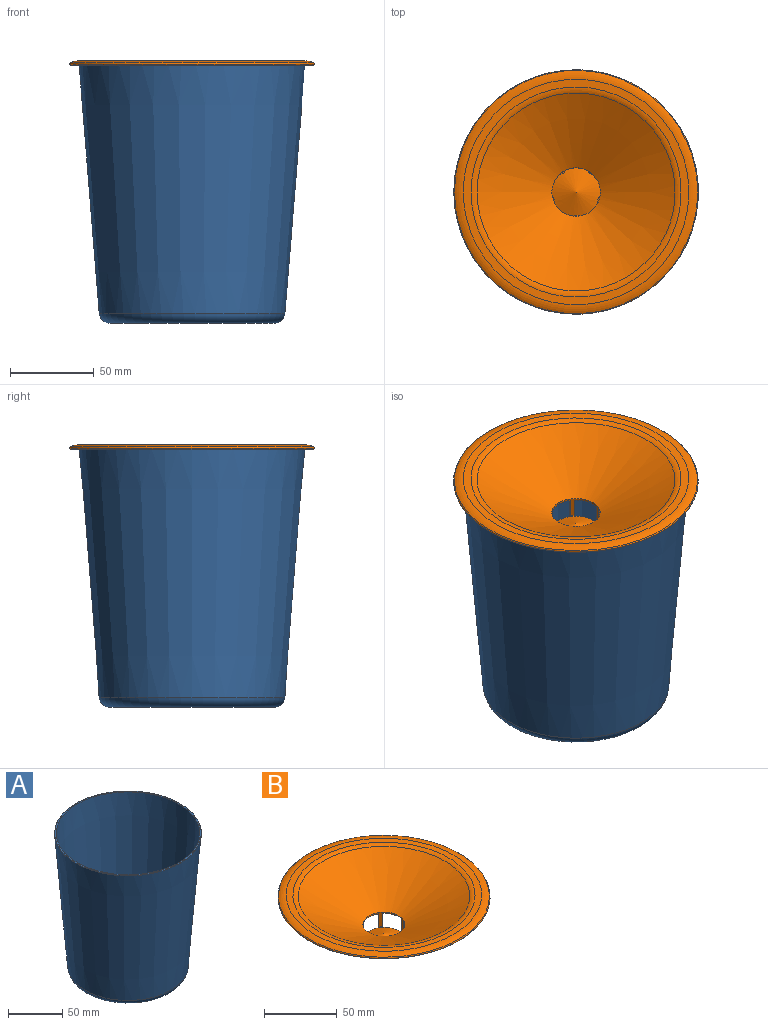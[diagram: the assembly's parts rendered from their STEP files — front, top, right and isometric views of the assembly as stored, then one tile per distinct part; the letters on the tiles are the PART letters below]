
ASSEMBLY  parts=2 mates=1
PART A: 8 faces, bbox 146.1x146.1x155 mm
  f0: plane 134.78x134.78mm, normal (0,0,1), area 583.2mm2, adj f1,f7
  f1: torus R=67.39mm, axis (0,0,-1), area 70mm2, adj f0,f2
  f2: cone r=67.49mm half-angle=4.6deg, axis (0,0,1), area 57717.2mm2, adj f1,f3
  f3: torus R=49mm, axis (0,0,-1), area 3226.7mm2, adj f2,f4
  f4: cone r=0mm half-angle=88.2deg, axis (0,0,-1), area 7547.4mm2, adj f3
  f5: cone r=48.89mm half-angle=88.2deg, axis (0,0,-1), area 7512.9mm2, adj f6
  f6: torus R=48.89mm, axis (0,0,-1), area 2432.2mm2, adj f5,f7
  f7: cone r=66mm half-angle=4.7deg, axis (0,0,1), area 56262.9mm2, adj f0,f6
PART B: 53 faces, bbox 163.4x163.4x39.1 mm
  f0: cylinder r=15.96mm len=11.08mm, axis (0,0,-1), area 30.9mm2, adj f4,f20,f32,f45
  f1: cylinder r=15.96mm len=11.08mm, axis (0,0,-1), area 30.9mm2, adj f4,f20,f28,f41
  f2: cylinder r=15.96mm len=11.08mm, axis (0,0,-1), area 30.9mm2, adj f4,f20,f37,f40
  f3: cylinder r=15.96mm len=11.08mm, axis (0,0,-1), area 30.9mm2, adj f4,f20,f33,f36
  f4: torus R=13.96mm, axis (0,0,-1), area 139.3mm2, adj f0,f1,f2,f3,f21,f22,f28,f29
  f5: torus R=67.32mm, axis (0,0,-1), area 2417.6mm2, adj f6,f27
  f6: torus R=72.27mm, axis (0,0,-1), area 556.1mm2, adj f5,f7
  f7: cone r=72.89mm half-angle=31.4deg, axis (0,0,1), area 9.2mm2, adj f6,f8
  f8: torus R=72.26mm, axis (0,0,-1), area 505.5mm2, adj f7,f9
  f9: torus R=67.32mm, axis (0,0,-1), area 2058.4mm2, adj f8,f10
  f10: torus R=67.4mm, axis (0,0,-1), area 66.8mm2, adj f9,f11
  f11: cylinder r=67.3mm len=134.6mm, axis (0,0,-1), area 338.2mm2, adj f10,f12
  f12: torus R=67.2mm, axis (0,0,-1), area 66.4mm2, adj f11,f13
  f13: plane 134.4x134.4mm, normal (0,0,-1), area 335.8mm2, adj f12,f14
  f14: torus R=66.4mm, axis (0,0,-1), area 65.5mm2, adj f13,f15
  f15: cylinder r=66.3mm len=132.6mm, axis (0,0,-1), area 333.3mm2, adj f14,f16
  f16: torus R=66.2mm, axis (0,0,-1), area 65.4mm2, adj f15,f17
  f17: plane 132.4x132.4mm, normal (0,0,-1), area 1362.4mm2, adj f16,f18
  f18: torus R=62.84mm, axis (0,0,-1), area 1229.4mm2, adj f17,f19
  f19: cone r=16.22mm half-angle=61.9deg, axis (0,0,1), area 11792.2mm2, adj f18,f20
  f20: torus R=16.46mm, axis (0,0,-1), area 54.4mm2, adj f0,f1,f2,f3,f19,f21,f31,f35
  f21: cylinder r=15.96mm len=11.08mm, axis (0,0,-1), area 30.9mm2, adj f4,f20,f29,f44
  f22: cone r=13.28mm half-angle=70.4deg, axis (0,0,-1), area 588.7mm2, adj f4
  f23: cone r=0mm half-angle=70.4deg, axis (0,0,-1), area 688.4mm2, adj f28,f29,f30,f32,f33,f34,f36,f37
  f24: cylinder r=14.46mm len=28.91mm, axis (0,0,-1), area 239.8mm2, adj f25,f28,f29,f31,f32,f33,f35,f36
  f25: cone r=14.46mm half-angle=61.9deg, axis (0,0,1), area 11693.6mm2, adj f24,f26
  f26: torus R=62.86mm, axis (0,0,-1), area 1443.6mm2, adj f25,f27
  f27: cone r=67.32mm half-angle=88.9deg, axis (0,0,1), area 1887.5mm2, adj f5,f26
  f28: plane 13.02x2mm, normal (-0.39,-0.92,0), area 18.9mm2, adj f1,f4,f23,f24,f30,f31,f50
  f29: plane 13.02x2.16mm, normal (1,0.09,0), area 18.9mm2, adj f4,f21,f23,f24,f30,f31,f49
  f30: cylinder r=14.46mm len=12.05mm, axis (0,0,-1), area 19.2mm2, adj f4,f23,f28,f29
  f31: plane 13.43x10.25mm, normal (0,0,-1), area 24.7mm2, adj f20,f24,f28,f29
  f32: plane 13.02x2.11mm, normal (-0.22,0.97,0), area 18.9mm2, adj f0,f4,f23,f24,f34,f35,f48
  f33: plane 13.02x1.64mm, normal (-0.75,-0.66,0), area 18.9mm2, adj f3,f4,f23,f24,f34,f35,f52
  f34: cylinder r=14.46mm len=14.16mm, axis (0,0,-1), area 19.2mm2, adj f4,f23,f32,f33
  f35: plane 15.63x6.47mm, normal (0,0,-1), area 24.7mm2, adj f20,f24,f32,f33
  f36: plane 13.02x1.86mm, normal (0.86,0.52,0), area 18.9mm2, adj f3,f4,f23,f24,f38,f39,f52
  f37: plane 13.02x1.86mm, normal (-0.86,0.52,0), area 18.9mm2, adj f2,f4,f23,f24,f38,f39,f51
  f38: cylinder r=14.46mm len=14.89mm, axis (0,0,-1), area 19.2mm2, adj f4,f23,f36,f37
  f39: plane 16.44x3.57mm, normal (0,0,-1), area 24.7mm2, adj f20,f24,f36,f37
  f40: plane 13.02x1.64mm, normal (0.75,-0.66,0), area 18.9mm2, adj f2,f4,f23,f24,f42,f43,f51
  f41: plane 13.02x2.11mm, normal (0.22,0.97,0), area 18.9mm2, adj f1,f4,f23,f24,f42,f43,f50
  f42: cylinder r=14.46mm len=14.16mm, axis (0,0,-1), area 19.2mm2, adj f4,f23,f40,f41
  f43: plane 15.63x6.47mm, normal (0,0,-1), area 24.7mm2, adj f20,f24,f40,f41
  f44: plane 13.02x2.16mm, normal (-1,0.09,0), area 18.9mm2, adj f4,f21,f23,f24,f46,f47,f49
  f45: plane 13.02x2mm, normal (0.39,-0.92,0), area 18.9mm2, adj f0,f4,f23,f24,f46,f47,f48
  f46: cylinder r=14.46mm len=12.05mm, axis (0,0,-1), area 19.2mm2, adj f4,f23,f44,f45
  f47: plane 13.43x10.25mm, normal (0,0,-1), area 24.7mm2, adj f20,f24,f44,f45
  f48: torus R=13.96mm, axis (0,0,-1), area 2.4mm2, adj f23,f24,f32,f45
  f49: torus R=13.96mm, axis (0,0,-1), area 2.4mm2, adj f23,f24,f29,f44
  f50: torus R=13.96mm, axis (0,0,-1), area 2.4mm2, adj f23,f24,f28,f41
  f51: torus R=13.96mm, axis (0,0,-1), area 2.4mm2, adj f23,f24,f37,f40
  f52: torus R=13.96mm, axis (0,0,-1), area 2.4mm2, adj f23,f24,f33,f36
PLACE A t=(-23.77,-8.04,-68.98)mm
PLACE B t=(-23.77,-8.04,48.62)mm
MATE revolute B.f22 <-> A.f1  axis (0,0,-1) through (-23.77,-8.04,86.02)mm
